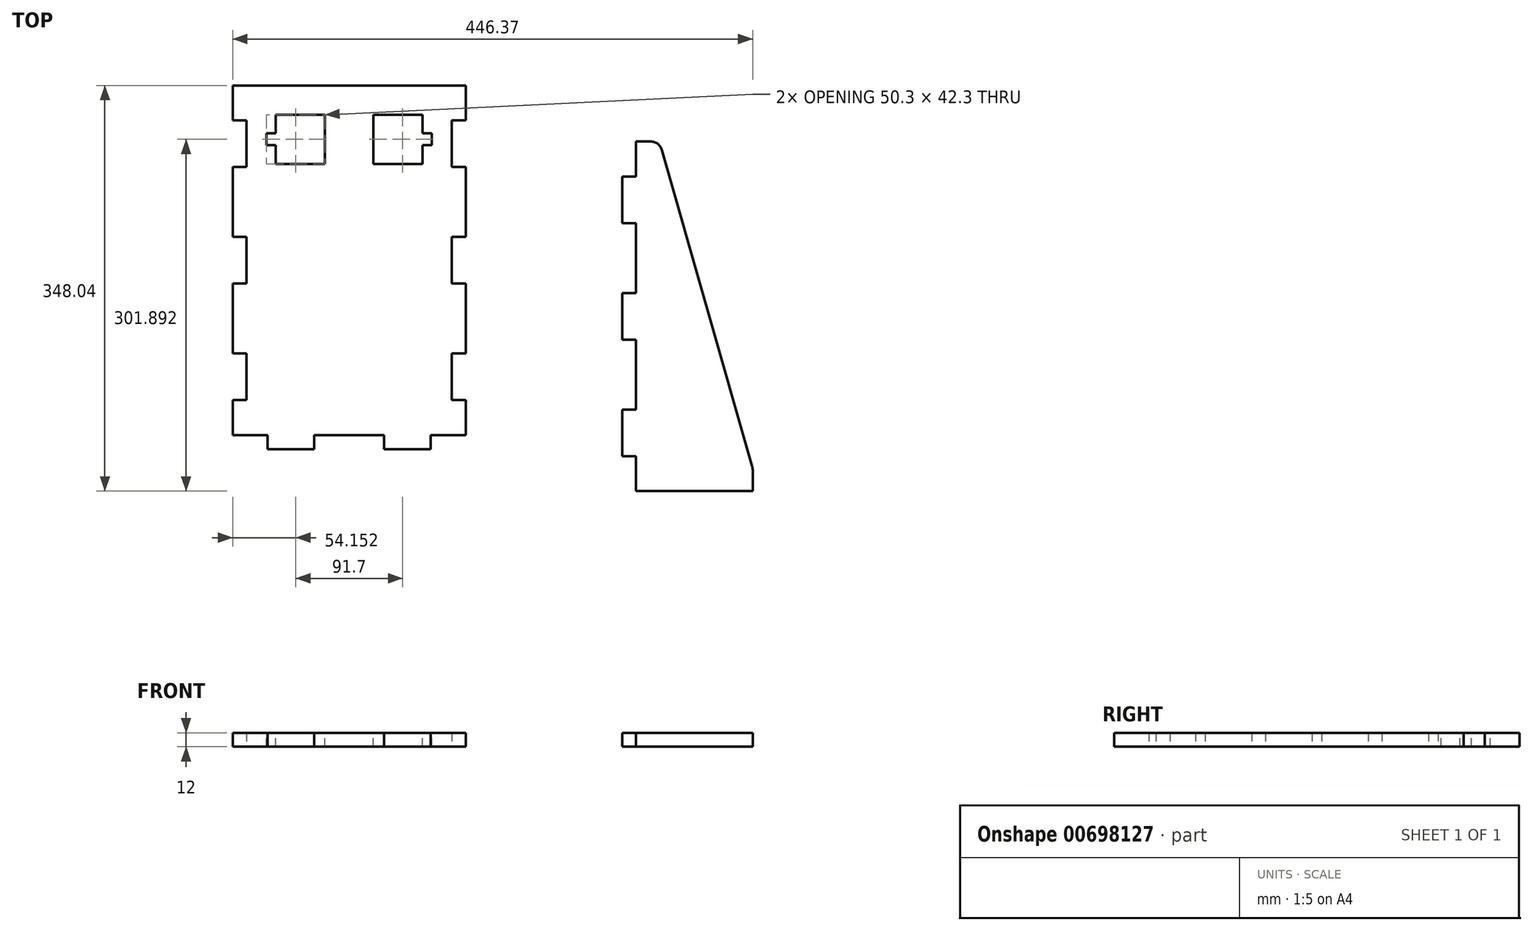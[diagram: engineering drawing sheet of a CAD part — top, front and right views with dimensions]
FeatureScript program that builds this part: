
annotation { "Feature Type Name" : "Feature", "Feature Type Description" : "" }
export const myFeature = defineFeature(function(context is Context, id is Id, definition is map)
    precondition{}
    {
        {
            assignVariable(context, id + "F0", {"name" : "wood", "anyValue" : 12 * mm});
        }
        {
            var Q0;
            Q0=qCreatedBy(makeId("Top.planeOp"),FACE);
            var sketch = newSketch(context, id + "F1", { "sketchPlane" : qUnion([Q0])});
            skLineSegment(sketch, "E0", {"start": v(-4.7, 79.94) * mm, "end": v(-4.7, -220.06) * mm});
            skLineSegment(sketch, "E1", {"start": v(-4.7, -220.06) * mm, "end": v(95.3, -220.06) * mm});
            skLineSegment(sketch, "E2", {"start": v(95.3, -220.06) * mm, "end": v(95.3, -200.06) * mm});
            skLineSegment(sketch, "E3", {"start": v(95.3, -200.06) * mm, "end": v(15.3, 79.94) * mm});
            skLineSegment(sketch, "E4", {"start": v(15.3, 79.94) * mm, "end": v(-4.7, 79.94) * mm});
            skLineSegment(sketch, "E5.bottom", {"start": v(-4.7, -220.06) * mm, "end": v(25.3, -220.06) * mm});
            skLineSegment(sketch, "E5.top", {"start": v(-4.7, -232.06) * mm, "end": v(25.3, -232.06) * mm});
            skLineSegment(sketch, "E5.left", {"start": v(-4.7, -220.06) * mm, "end": v(-4.7, -232.06) * mm});
            skLineSegment(sketch, "E5.right", {"start": v(25.3, -220.06) * mm, "end": v(25.3, -232.06) * mm});
            skLineSegment(sketch, "E6.bottom", {"start": v(95.3, -220.06) * mm, "end": v(65.3, -220.06) * mm});
            skLineSegment(sketch, "E6.top", {"start": v(95.3, -232.06) * mm, "end": v(65.3, -232.06) * mm});
            skLineSegment(sketch, "E6.left", {"start": v(95.3, -220.06) * mm, "end": v(95.3, -232.06) * mm});
            skLineSegment(sketch, "E6.right", {"start": v(65.3, -220.06) * mm, "end": v(65.3, -232.06) * mm});
            skPoint(sketch, "E7", {"position": v(-4.7, 29.94) * mm});
            skPoint(sketch, "E8", {"position": v(-4.7, -170.06) * mm});
            skLineSegment(sketch, "E9.bottom", {"start": v(7.3, 9.94) * mm, "end": v(-16.7, 9.94) * mm});
            skLineSegment(sketch, "E9.top", {"start": v(7.3, 49.94) * mm, "end": v(-16.7, 49.94) * mm});
            skLineSegment(sketch, "E9.left", {"start": v(7.3, 9.94) * mm, "end": v(7.3, 49.94) * mm});
            skLineSegment(sketch, "E9.right", {"start": v(-16.7, 9.94) * mm, "end": v(-16.7, 49.94) * mm});
            skLineSegment(sketch, "E10.bottom", {"start": v(7.3, -150.06) * mm, "end": v(-16.7, -150.06) * mm});
            skLineSegment(sketch, "E10.top", {"start": v(7.3, -190.06) * mm, "end": v(-16.7, -190.06) * mm});
            skLineSegment(sketch, "E10.left", {"start": v(7.3, -150.06) * mm, "end": v(7.3, -190.06) * mm});
            skLineSegment(sketch, "E10.right", {"start": v(-16.7, -150.06) * mm, "end": v(-16.7, -190.06) * mm});
            skLineSegment(sketch, "E11.bottom", {"start": v(7.3, -90.06) * mm, "end": v(-16.7, -90.06) * mm});
            skLineSegment(sketch, "E11.top", {"start": v(7.3, -50.06) * mm, "end": v(-16.7, -50.06) * mm});
            skLineSegment(sketch, "E11.left", {"start": v(7.3, -90.06) * mm, "end": v(7.3, -50.06) * mm});
            skLineSegment(sketch, "E11.right", {"start": v(-16.7, -90.06) * mm, "end": v(-16.7, -50.06) * mm});
            skPoint(sketch, "E11.middle", {"position": v(-4.7, -70.06) * mm});
            skSolve(sketch);
        }
        {
            var Q0;
            {var subQ5=sQuery(id+"F1.wireOp",EDGE,"E9.right");Q0=makeQuery(id+"F1.imprint","IMPRINT",FACE,{"disambiguationData":[TD([[makeQuery(id+"F1.imprint","IMPRINT",EDGE,{"derivedFrom":subQ5}),-1.0]])]});}
            var Q1;
            Q1=makeQuery(id+"F1.imprint","IMPRINT",FACE,{"disambiguationData":[TD([[makeQuery(id+"F1.imprint","IMPRINT",EDGE,{"derivedFrom":sQuery(id+"F1.wireOp",EDGE,"E6.bottom")}),1.0]])]});
            var Q2;
            Q2=makeQuery(id+"F1.imprint","IMPRINT",FACE,{"disambiguationData":[TD([[makeQuery(id+"F1.imprint","IMPRINT",EDGE,{"derivedFrom":sQuery(id+"F1.wireOp",EDGE,"E5.bottom")}),-1.0]])]});
            var Q3;
            {var subQ5=sQuery(id+"F1.wireOp",EDGE,"E10.right");Q3=makeQuery(id+"F1.imprint","IMPRINT",FACE,{"disambiguationData":[TD([[makeQuery(id+"F1.imprint","IMPRINT",EDGE,{"derivedFrom":subQ5}),1.0]])]});}
            var Q4;
            {var subQ5=sQuery(id+"F1.wireOp",EDGE,"E9.left");Q4=makeQuery(id+"F1.imprint","IMPRINT",FACE,{"disambiguationData":[TD([[makeQuery(id+"F1.imprint","IMPRINT",EDGE,{"derivedFrom":subQ5}),1.0]])]});}
            var Q5;
            {var subQ5=sQuery(id+"F1.wireOp",EDGE,"E10.left");Q5=makeQuery(id+"F1.imprint","IMPRINT",FACE,{"disambiguationData":[TD([[makeQuery(id+"F1.imprint","IMPRINT",EDGE,{"derivedFrom":subQ5}),-1.0]])]});}
            var Q6;
            Q6=makeQuery(id+"F1.imprint","IMPRINT",FACE,{"disambiguationData":[TD([[makeQuery(id+"F1.imprint","IMPRINT",EDGE,{"derivedFrom":sQuery(id+"F1.wireOp",EDGE,"E1")}),1.0]])]});
            var Q7;
            {var subQ5=sQuery(id+"F1.wireOp",EDGE,"E11.left");Q7=makeQuery(id+"F1.imprint","IMPRINT",FACE,{"disambiguationData":[TD([[makeQuery(id+"F1.imprint","IMPRINT",EDGE,{"derivedFrom":subQ5}),1.0]])]});}
            var Q8;
            {var subQ5=sQuery(id+"F1.wireOp",EDGE,"E11.right");Q8=makeQuery(id+"F1.imprint","IMPRINT",FACE,{"disambiguationData":[TD([[makeQuery(id+"F1.imprint","IMPRINT",EDGE,{"derivedFrom":subQ5}),-1.0]])]});}
            extrude(context, id + "F2", {"entities" : qUnion([Q0, Q1, Q2, Q3, Q4, Q5, Q6, Q7, Q8]), "depth" : getVariable(context, 'wood'), "offsetDistance" : 25 * mm});
        }
        {
            var Q0;
            Q0=makeQuery(id+"F2.opExtrude","SWEPT_EDGE",EDGE,{"disambiguationData":[OSD([sQuery(id+"F1.wireOp",EDGE,"E2"),sQuery(id+"F1.wireOp",EDGE,"E3")])]});
            var Q1;
            Q1=makeQuery(id+"F2.opExtrude","SWEPT_EDGE",EDGE,{"disambiguationData":[OSD([sQuery(id+"F1.wireOp",EDGE,"E3"),sQuery(id+"F1.wireOp",EDGE,"E4")])]});
            fillet(context, id + "F3", {"entities" : qUnion([Q0, Q1]), "radius" : 10 * mm, "tangentPropagation" : true, "allowEdgeOverflow" : false});
        }
        {
            var Q0;
            Q0=qCreatedBy(makeId("Top.planeOp"),FACE);
            var sketch = newSketch(context, id + "F4", { "sketchPlane" : qUnion([Q0])});
            skLineSegment(sketch, "E12.bottom", {"start": v(-151.08, -172.02) * mm, "end": v(-351.08, -172.02) * mm});
            skLineSegment(sketch, "E12.top", {"start": v(-151.08, 127.98) * mm, "end": v(-351.08, 127.98) * mm});
            skLineSegment(sketch, "E12.left", {"start": v(-151.08, -172.02) * mm, "end": v(-151.08, -142.02) * mm});
            skLineSegment(sketch, "E12.right", {"start": v(-351.08, -172.02) * mm, "end": v(-351.08, -142.02) * mm});
            skPoint(sketch, "E12.middle", {"position": v(-251.08, -22.02) * mm});
            skLineSegment(sketch, "E13", {"start": v(-371.07, -22.02) * mm, "end": v(-201.73, -22.02) * mm, "construction": true});
            skLineSegment(sketch, "E14", {"start": v(-251.08, 72.16) * mm, "end": v(-251.08, -155.56) * mm, "construction": true});
            skLineSegment(sketch, "E15.bottom", {"start": v(-339.08, -142.02) * mm, "end": v(-351.08, -142.02) * mm});
            skLineSegment(sketch, "E15.top", {"start": v(-339.08, -102.02) * mm, "end": v(-351.08, -102.02) * mm});
            skLineSegment(sketch, "E15.left", {"start": v(-339.08, -142.02) * mm, "end": v(-339.08, -102.02) * mm});
            skPoint(sketch, "E15.middle", {"position": v(-351.08, -122.02) * mm});
            skPoint(sketch, "E15.right.end.orphan", {"position": v(-363.08, -102.02) * mm});
            skPoint(sketch, "E16.orphan", {"position": v(-363.08, -142.02) * mm});
            skLineSegment(sketch, "E17.trimOffspring", {"start": v(-351.08, -102.02) * mm, "end": v(-351.08, -42.02) * mm});
            skLineSegment(sketch, "E18.MirrorCS", {"start": v(-163.08, -142.02) * mm, "end": v(-163.08, -102.02) * mm});
            skPoint(sketch, "E19.MirrorP", {"position": v(-139.08, -102.02) * mm});
            skPoint(sketch, "E20.MirrorP", {"position": v(-139.08, -142.02) * mm});
            skLineSegment(sketch, "E21.MirrorCS", {"start": v(-163.08, -142.02) * mm, "end": v(-151.08, -142.02) * mm});
            skLineSegment(sketch, "E22.MirrorCS", {"start": v(-163.08, -102.02) * mm, "end": v(-151.08, -102.02) * mm});
            skPoint(sketch, "E23.MirrorP", {"position": v(-151.08, -122.02) * mm});
            skLineSegment(sketch, "E24.MirrorCS", {"start": v(-131.08, -22.02) * mm, "end": v(-300.42, -22.02) * mm, "construction": true});
            skPoint(sketch, "E25.MirrorP", {"position": v(-139.08, 97.98) * mm});
            skPoint(sketch, "E26.MirrorP", {"position": v(-139.08, 57.98) * mm});
            skPoint(sketch, "E27.MirrorP", {"position": v(-151.08, 77.98) * mm});
            skLineSegment(sketch, "E28.MirrorCS", {"start": v(-163.08, 97.98) * mm, "end": v(-163.08, 57.98) * mm});
            skLineSegment(sketch, "E29.MirrorCS", {"start": v(-163.08, 57.98) * mm, "end": v(-151.08, 57.98) * mm});
            skLineSegment(sketch, "E30.MirrorCS", {"start": v(-163.08, 97.98) * mm, "end": v(-151.08, 97.98) * mm});
            skLineSegment(sketch, "E31.MirrorCS", {"start": v(-339.08, 97.98) * mm, "end": v(-351.08, 97.98) * mm});
            skPoint(sketch, "E32.MirrorP", {"position": v(-363.08, 57.98) * mm});
            skLineSegment(sketch, "E33.MirrorCS", {"start": v(-339.08, 97.98) * mm, "end": v(-339.08, 57.98) * mm});
            skLineSegment(sketch, "E34.MirrorCS", {"start": v(-339.08, 57.98) * mm, "end": v(-351.08, 57.98) * mm});
            skPoint(sketch, "E35.MirrorP", {"position": v(-363.08, 97.98) * mm});
            skPoint(sketch, "E36.MirrorP", {"position": v(-351.08, 77.98) * mm});
            skLineSegment(sketch, "E37.trimOffspring", {"start": v(-351.08, 97.98) * mm, "end": v(-351.08, 127.98) * mm});
            skLineSegment(sketch, "E38.trimOffspring", {"start": v(-151.08, 97.98) * mm, "end": v(-151.08, 127.98) * mm});
            skLineSegment(sketch, "E39.trimOffspring", {"start": v(-151.08, -102.02) * mm, "end": v(-151.08, -42.02) * mm});
            skLineSegment(sketch, "E40.bottom", {"start": v(-281.08, -184.02) * mm, "end": v(-321.08, -184.02) * mm});
            skLineSegment(sketch, "E40.top", {"start": v(-281.08, -160.02) * mm, "end": v(-321.08, -160.02) * mm});
            skLineSegment(sketch, "E40.left", {"start": v(-281.08, -184.02) * mm, "end": v(-281.08, -160.02) * mm});
            skLineSegment(sketch, "E40.right", {"start": v(-321.08, -184.02) * mm, "end": v(-321.08, -160.02) * mm});
            skPoint(sketch, "E40.middle", {"position": v(-301.08, -172.02) * mm});
            skPoint(sketch, "E41.MirrorP", {"position": v(-201.08, -172.02) * mm});
            skLineSegment(sketch, "E42.MirrorCS", {"start": v(-221.08, -160.02) * mm, "end": v(-181.08, -160.02) * mm});
            skLineSegment(sketch, "E43.MirrorCS", {"start": v(-221.08, -184.02) * mm, "end": v(-181.08, -184.02) * mm});
            skLineSegment(sketch, "E44.MirrorCS", {"start": v(-181.08, -184.02) * mm, "end": v(-181.08, -160.02) * mm});
            skLineSegment(sketch, "E45.MirrorCS", {"start": v(-221.08, -184.02) * mm, "end": v(-221.08, -160.02) * mm});
            skLineSegment(sketch, "E46.bottom", {"start": v(-339.08, -42.02) * mm, "end": v(-351.08, -42.02) * mm});
            skLineSegment(sketch, "E46.top", {"start": v(-339.08, -2.02) * mm, "end": v(-351.08, -2.02) * mm});
            skLineSegment(sketch, "E46.left", {"start": v(-339.08, -42.02) * mm, "end": v(-339.08, -2.02) * mm});
            skPoint(sketch, "E46.middle", {"position": v(-351.08, -22.02) * mm});
            skPoint(sketch, "E47.orphan", {"position": v(-363.08, -2.02) * mm});
            skPoint(sketch, "E48.orphan", {"position": v(-363.08, -42.02) * mm});
            skLineSegment(sketch, "E49.trimOffspring", {"start": v(-351.08, -2.02) * mm, "end": v(-351.08, 57.98) * mm});
            skLineSegment(sketch, "E50.MirrorCS", {"start": v(-163.08, -42.02) * mm, "end": v(-151.08, -42.02) * mm});
            skLineSegment(sketch, "E51.MirrorCS", {"start": v(-163.08, -42.02) * mm, "end": v(-163.08, -2.02) * mm});
            skLineSegment(sketch, "E52.MirrorCS", {"start": v(-163.08, -2.02) * mm, "end": v(-151.08, -2.02) * mm});
            skPoint(sketch, "E53.MirrorP", {"position": v(-139.08, -42.02) * mm});
            skPoint(sketch, "E54.MirrorP", {"position": v(-139.08, -2.02) * mm});
            skPoint(sketch, "E55.MirrorP", {"position": v(-151.08, -22.02) * mm});
            skLineSegment(sketch, "E56.trimOffspring", {"start": v(-151.08, -2.02) * mm, "end": v(-151.08, 57.98) * mm});
            skSolve(sketch);
        }
        {
            var Q0;
            {var subQ5=sQuery(id+"F4.wireOp",EDGE,"E43.MirrorCS");Q0=makeQuery(id+"F4.imprint","IMPRINT",FACE,{"disambiguationData":[TD([[makeQuery(id+"F4.imprint","IMPRINT",EDGE,{"derivedFrom":subQ5}),1.0]])]});}
            var Q1;
            {var subQ5=sQuery(id+"F4.wireOp",EDGE,"E40.bottom");Q1=makeQuery(id+"F4.imprint","IMPRINT",FACE,{"disambiguationData":[TD([[makeQuery(id+"F4.imprint","IMPRINT",EDGE,{"derivedFrom":subQ5}),-1.0]])]});}
            var Q2;
            Q2=makeQuery(id+"F4.imprint","IMPRINT",FACE,{"disambiguationData":[TD([[makeQuery(id+"F4.imprint","IMPRINT",EDGE,{"derivedFrom":sQuery(id+"F4.wireOp",EDGE,"E12.top")}),1.0]])]});
            var Q3;
            {var subQ5=sQuery(id+"F4.wireOp",EDGE,"E42.MirrorCS");Q3=makeQuery(id+"F4.imprint","IMPRINT",FACE,{"disambiguationData":[TD([[makeQuery(id+"F4.imprint","IMPRINT",EDGE,{"derivedFrom":subQ5}),-1.0]])]});}
            var Q4;
            {var subQ5=sQuery(id+"F4.wireOp",EDGE,"E40.top");Q4=makeQuery(id+"F4.imprint","IMPRINT",FACE,{"disambiguationData":[TD([[makeQuery(id+"F4.imprint","IMPRINT",EDGE,{"derivedFrom":subQ5}),1.0]])]});}
            extrude(context, id + "F5", {"entities" : qUnion([Q0, Q1, Q2, Q3, Q4]), "depth" : getVariable(context, 'wood'), "offsetDistance" : 25 * mm});
        }
        {
            var Q0;
            Q0=makeQuery(id+"F5.opExtrude","CAP_FACE",FACE,{"disambiguationData":[OSD([sQuery(id+"F4.wireOp",EDGE,"E12.bottom"),sQuery(id+"F4.wireOp",EDGE,"E12.top"),sQuery(id+"F4.wireOp",EDGE,"E12.left"),sQuery(id+"F4.wireOp",EDGE,"E12.right"),sQuery(id+"F4.wireOp",EDGE,"E15.bottom"),sQuery(id+"F4.wireOp",EDGE,"E15.top"),sQuery(id+"F4.wireOp",EDGE,"E15.left"),sQuery(id+"F4.wireOp",EDGE,"E17.trimOffspring"),sQuery(id+"F4.wireOp",EDGE,"E18.MirrorCS"),sQuery(id+"F4.wireOp",EDGE,"E21.MirrorCS"),sQuery(id+"F4.wireOp",EDGE,"E22.MirrorCS"),sQuery(id+"F4.wireOp",EDGE,"E28.MirrorCS"),sQuery(id+"F4.wireOp",EDGE,"E29.MirrorCS"),sQuery(id+"F4.wireOp",EDGE,"E30.MirrorCS"),sQuery(id+"F4.wireOp",EDGE,"E31.MirrorCS"),sQuery(id+"F4.wireOp",EDGE,"E33.MirrorCS"),sQuery(id+"F4.wireOp",EDGE,"E34.MirrorCS"),sQuery(id+"F4.wireOp",EDGE,"E37.trimOffspring"),sQuery(id+"F4.wireOp",EDGE,"E38.trimOffspring"),sQuery(id+"F4.wireOp",EDGE,"E39.trimOffspring"),sQuery(id+"F4.wireOp",EDGE,"E40.bottom"),sQuery(id+"F4.wireOp",EDGE,"E40.left"),sQuery(id+"F4.wireOp",EDGE,"E40.right"),sQuery(id+"F4.wireOp",EDGE,"E43.MirrorCS"),sQuery(id+"F4.wireOp",EDGE,"E44.MirrorCS"),sQuery(id+"F4.wireOp",EDGE,"E45.MirrorCS")])],"isStart":false});
            var sketch = newSketch(context, id + "F6", { "sketchPlane" : qUnion([Q0])});
            skLineSegment(sketch, "E57.bottom", {"start": v(-314.08, 102.98) * mm, "end": v(-271.78, 102.98) * mm});
            skLineSegment(sketch, "E57.top", {"start": v(-314.08, 60.68) * mm, "end": v(-271.78, 60.68) * mm});
            skLineSegment(sketch, "E57.left", {"start": v(-314.08, 102.98) * mm, "end": v(-314.08, 60.68) * mm});
            skLineSegment(sketch, "E57.right", {"start": v(-271.78, 102.98) * mm, "end": v(-271.78, 60.68) * mm});
            skLineSegment(sketch, "E58.bottom", {"start": v(-306.08, 76.83) * mm, "end": v(-322.08, 76.83) * mm});
            skLineSegment(sketch, "E58.top", {"start": v(-306.08, 86.83) * mm, "end": v(-322.08, 86.83) * mm});
            skLineSegment(sketch, "E58.left", {"start": v(-306.08, 76.83) * mm, "end": v(-306.08, 86.83) * mm});
            skLineSegment(sketch, "E58.right", {"start": v(-322.08, 76.83) * mm, "end": v(-322.08, 86.83) * mm});
            skPoint(sketch, "E58.middle", {"position": v(-314.08, 81.83) * mm});
            skLineSegment(sketch, "E59.MirrorCS", {"start": v(-180.08, 76.83) * mm, "end": v(-180.08, 86.83) * mm});
            skLineSegment(sketch, "E60.MirrorCS", {"start": v(-196.08, 76.83) * mm, "end": v(-196.08, 86.83) * mm});
            skLineSegment(sketch, "E61.MirrorCS", {"start": v(-196.08, 86.83) * mm, "end": v(-180.08, 86.83) * mm});
            skLineSegment(sketch, "E62.MirrorCS", {"start": v(-188.08, 102.98) * mm, "end": v(-230.38, 102.98) * mm});
            skLineSegment(sketch, "E63.MirrorCS", {"start": v(-188.08, 60.68) * mm, "end": v(-230.38, 60.68) * mm});
            skLineSegment(sketch, "E64.MirrorCS", {"start": v(-188.08, 102.98) * mm, "end": v(-188.08, 60.68) * mm});
            skLineSegment(sketch, "E65.MirrorCS", {"start": v(-196.08, 76.83) * mm, "end": v(-180.08, 76.83) * mm});
            skLineSegment(sketch, "E66.MirrorCS", {"start": v(-230.38, 102.98) * mm, "end": v(-230.38, 60.68) * mm});
            skPoint(sketch, "E67.MirrorP", {"position": v(-188.08, 81.83) * mm});
            skSolve(sketch);
        }
        {
            var Q0;
            {var subQ5=sQuery(id+"F6.wireOp",EDGE,"E58.right");Q0=makeQuery(id+"F6.imprint","IMPRINT",FACE,{"disambiguationData":[TD([[makeQuery(id+"F6.imprint","IMPRINT",EDGE,{"derivedFrom":subQ5}),-1.0]])]});}
            var Q1;
            {var subQ4=sQuery(id+"F6.wireOp",EDGE,"E57.bottom");Q1=makeQuery(id+"F6.imprint","IMPRINT",FACE,{"disambiguationData":[TD([[makeQuery(id+"F6.imprint","IMPRINT",EDGE,{"derivedFrom":subQ4}),-1.0]])]});}
            var Q2;
            {var subQ5=sQuery(id+"F6.wireOp",EDGE,"E58.left");Q2=makeQuery(id+"F6.imprint","IMPRINT",FACE,{"disambiguationData":[TD([[makeQuery(id+"F6.imprint","IMPRINT",EDGE,{"derivedFrom":subQ5}),1.0]])]});}
            var Q3;
            {var subQ0=sQuery(id+"F6.wireOp",EDGE,"E60.MirrorCS");Q3=makeQuery(id+"F6.imprint","IMPRINT",FACE,{"disambiguationData":[TD([[makeQuery(id+"F6.imprint","IMPRINT",EDGE,{"derivedFrom":subQ0}),-1.0]])]});}
            var Q4;
            {var subQ3=sQuery(id+"F6.wireOp",EDGE,"E60.MirrorCS");Q4=makeQuery(id+"F6.imprint","IMPRINT",FACE,{"disambiguationData":[TD([[makeQuery(id+"F6.imprint","IMPRINT",EDGE,{"derivedFrom":subQ3}),1.0]])]});}
            var Q5;
            {var subQ0=sQuery(id+"F6.wireOp",EDGE,"E59.MirrorCS");Q5=makeQuery(id+"F6.imprint","IMPRINT",FACE,{"disambiguationData":[TD([[makeQuery(id+"F6.imprint","IMPRINT",EDGE,{"derivedFrom":subQ0}),1.0]])]});}
            extrude(context, id + "F7", {"entities" : qUnion([Q0, Q1, Q2, Q3, Q4, Q5]), "operationType" : NewBodyOperationType.REMOVE, "endBound" : BoundingType.UP_TO_NEXT, "oppositeDirection" : true, "depth" : 25 * mm, "offsetDistance" : 25 * mm});
        }
    });
